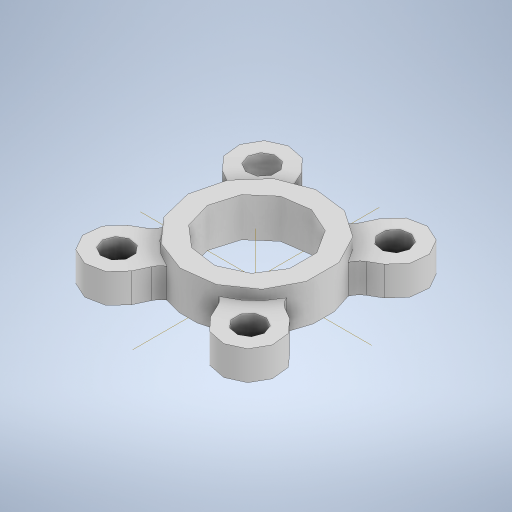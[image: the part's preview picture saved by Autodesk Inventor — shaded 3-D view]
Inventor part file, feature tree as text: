
AUTODESK INVENTOR PART (.ipt)
format: ipt  version: 2024.2 (Build 282272000, 272)  size: 301,056 bytes
history: native  units: mm
features: extrude x2, mirror x2, other x1, sketch x1
ambient origin geometry x8: Origin, YZ Plane, XZ Plane, XY Plane, X Axis, Y Axis, Z Axis, Center Point
bodies: Body1 (feature_tree)
feature tree (6):
  other  "Твердое тело1"
  sketch  "Эскиз1"
  extrude  "Выдавливание1"  Depth=10.0mm
  extrude  "Выдавливание2"  Depth=6.0mm
  mirror  "Зеркальное отражение1"
  mirror  "Зеркальное отражение2"
